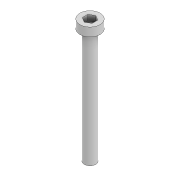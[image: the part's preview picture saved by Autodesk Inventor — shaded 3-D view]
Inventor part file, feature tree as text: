
AUTODESK INVENTOR PART (.ipt)
format: ipt  version: 2022 (Build 260153000, 153)  size: 91,648 bytes
history: native  units: mm
features: extrude x3, sketch x3
ambient origin geometry x8: Origin, YZ Plane, XZ Plane, XY Plane, X Axis, Y Axis, Z Axis, Center Point
bodies: Solid1 (feature_tree)
feature tree (6):
  extrude  "Extrusion1"  Depth=40.0mm TaperAngle=0.0deg
  extrude  "Extrusion2"  Depth=3.0mm TaperAngle=0.0deg
  extrude  "Extrusion3"  [1 undecoded]
  sketch  "Sketch1"  dims[d0=4.0mm d1=40.0mm d2=0.0mm]
  sketch  "Sketch2"  dims[d3=7.0mm d4=3.0mm d5=0.0mm]
  sketch  "Sketch3"  dims[d6=2.0mm d7=0.0mm]
note: 1 required parameter value undecoded (feature->parameter linkage not recoverable at this tier; creation-order binding heuristic only, values carry confidence <= 0.55)
